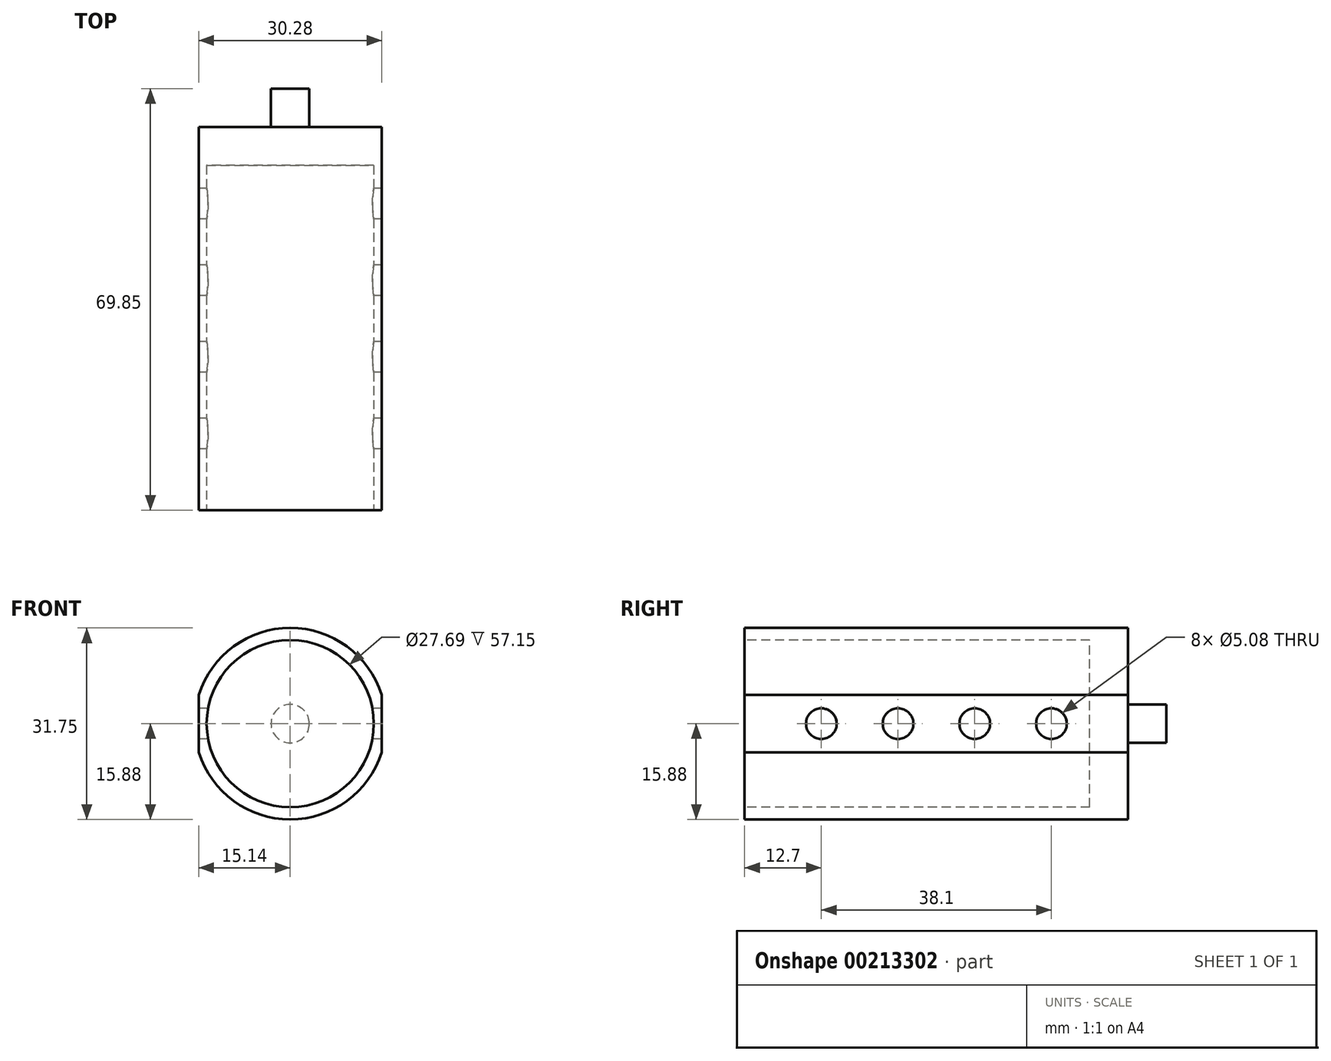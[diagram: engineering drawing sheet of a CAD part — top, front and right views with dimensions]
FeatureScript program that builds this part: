
annotation { "Feature Type Name" : "Feature", "Feature Type Description" : "" }
export const myFeature = defineFeature(function(context is Context, id is Id, definition is map)
    precondition{}
    {
        {
            var Q0;
            Q0=qCreatedBy(makeId("Front.planeOp"),FACE);
            var sketch = newSketch(context, id + "F0", { "sketchPlane" : qUnion([Q0])});
            skArc(sketch, "E0", {"start": v(15.14, 4.76) * mm, "mid": v(0, 15.88) * mm, "end": v(-15.14, 4.76) * mm});
            skLineSegment(sketch, "E1.left", {"start": v(-15.14, 4.76) * mm, "end": v(-15.14, -4.76) * mm});
            skLineSegment(sketch, "E1.right", {"start": v(15.14, 4.76) * mm, "end": v(15.14, -4.76) * mm});
            skArc(sketch, "E2.trimOffspring", {"start": v(-15.14, -4.76) * mm, "mid": v(0, -15.88) * mm, "end": v(15.14, -4.76) * mm});
            skSolve(sketch);
        }
        {
            var Q0;
            Q0 = qSketchRegion(id + "F0", true);
            extrude(context, id + "F1", {"entities" : qUnion([Q0]), "depth" : 63.5 * mm});
        }
        {
            var Q0;
            Q0=makeQuery(id+"F1.opExtrude","CAP_FACE",FACE,{"disambiguationData":[OSD([sQuery(id+"F0.wireOp",EDGE,"E0"),sQuery(id+"F0.wireOp",EDGE,"E1.left"),sQuery(id+"F0.wireOp",EDGE,"E1.right"),sQuery(id+"F0.wireOp",EDGE,"E2.trimOffspring")])],"isStart":false});
            var sketch = newSketch(context, id + "F2", { "sketchPlane" : qUnion([Q0])});
            skCircle(sketch, "E3", {"center": v(0, 0) * mm, "radius": 13.84 * mm});
            skSolve(sketch);
        }
        {
            var Q0;
            Q0 = qSketchRegion(id + "F2", true);
            extrude(context, id + "F3", {"entities" : qUnion([Q0]), "operationType" : NewBodyOperationType.REMOVE, "oppositeDirection" : true, "depth" : 57.15 * mm});
        }
        {
            var Q0;
            Q0=makeQuery(id+"F1.opExtrude","CAP_FACE",FACE,{"disambiguationData":[OSD([sQuery(id+"F0.wireOp",EDGE,"E0"),sQuery(id+"F0.wireOp",EDGE,"E1.left"),sQuery(id+"F0.wireOp",EDGE,"E1.right"),sQuery(id+"F0.wireOp",EDGE,"E2.trimOffspring")])],"isStart":true});
            var sketch = newSketch(context, id + "F4", { "sketchPlane" : qUnion([Q0])});
            skCircle(sketch, "E4", {"center": v(0, 0) * mm, "radius": 3.18 * mm});
            skSolve(sketch);
        }
        {
            var Q0;
            Q0 = qSketchRegion(id + "F4", true);
            extrude(context, id + "F5", {"entities" : qUnion([Q0]), "operationType" : NewBodyOperationType.ADD, "depth" : 6.35 * mm});
        }
        {
            var Q0;
            Q0=makeQuery(id+"F1.opExtrude","SWEPT_FACE",FACE,{"disambiguationData":[OSD([sQuery(id+"F0.wireOp",EDGE,"E1.left")])]});
            var sketch = newSketch(context, id + "F6", { "sketchPlane" : qUnion([Q0])});
            skCircle(sketch, "E5", {"center": v(12.7, 0) * mm, "radius": 2.54 * mm});
            skCircle(sketch, "E6", {"center": v(50.8, 0) * mm, "radius": 2.54 * mm});
            skCircle(sketch, "E7", {"center": v(25.4, 0) * mm, "radius": 2.54 * mm});
            skCircle(sketch, "E8", {"center": v(38.1, 0) * mm, "radius": 2.54 * mm});
            skSolve(sketch);
        }
        {
            var Q0;
            Q0 = qSketchRegion(id + "F6", true);
            extrude(context, id + "F7", {"entities" : qUnion([Q0]), "operationType" : NewBodyOperationType.REMOVE, "endBound" : BoundingType.THROUGH_ALL, "oppositeDirection" : true, "depth" : 25.4 * mm});
        }
    });
